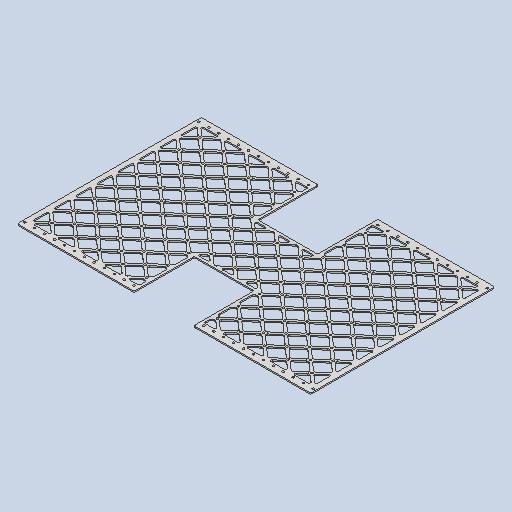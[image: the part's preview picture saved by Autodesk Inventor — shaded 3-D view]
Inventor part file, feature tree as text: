
AUTODESK INVENTOR PART (.ipt)
format: ipt  version: 2023 (Build 270158000, 158)  size: 3,945,984 bytes
history: native  units: in
note: dims shown in document units (in); Inventor stores cm internally (conversion verified against a paired STEP export)
features: extrude x10, sketch x6, pattern_linear x3, fillet x2, plane x1, mirror x1
ambient origin geometry x8: Origin, YZ Plane, XZ Plane, XY Plane, X Axis, Y Axis, Z Axis, Center Point
bodies: Solid1 (feature_tree)
feature tree (23):
  extrude  "Extrusion1"  Depth=0.5in
  sketch  "Sketch2"  dims[d6=0.25in d7=0.5in]
  extrude  "Extrusion2"  Depth=0.5in
  pattern_linear  "Rectangular Pattern1"  Spacing1=2.125in  [1 undecoded]
  extrude  "Extrusion3"  Depth=0.25in
  sketch  "Sketch4"  dims[d10=17.0in]
  sketch  "Sketch7"  dims[d11=28.5in]
  extrude  "Extrusion10"  Depth=0.25in
  extrude  "Extrusion11"  TaperAngle=0.0deg  [1 undecoded]
  extrude  "Extrusion12"  Depth=0.125in
  extrude  "Extrusion13"  Depth=0.125in
  pattern_linear  "Rectangular Pattern2"  Spacing1=0.5in  [1 undecoded]
  pattern_linear  "Rectangular Pattern3"  Spacing1=0.5in  [1 undecoded]
  extrude  "Extrusion7"  TaperAngle=0.0deg  [1 undecoded]
  extrude  "Extrusion8"  Depth=0.25in
  plane  "Work Plane2"
  extrude  "Extrusion14"  Depth=0.25in
  mirror  "Mirror3"
  fillet  "Fillet1"  Radius=0.25in
  fillet  "Fillet2"  Radius=0.25in
  sketch  "Sketch1"  dims[d2=0.25in d4=0.5in]
  sketch  "Sketch3"  dims[d8=0.125in d9=0.0in]
  sketch  "Sketch8"  dims[d12=2.375in d13=2.125in d14=0.25in d15=0.25in d16=0.0in d17=0.0in d18=3.1496in d20=2.125in d21=4.7244in d23=-2.375in d24=0.5in d25=0.5in d26=0.0in d27=0.0in d32=0.25in d40=0.25in d41=0.25in d42=0.25in d43=0.0in d44=0.0in d45=0.0in d46=0.0in d49=0.21in d50=0.5in d51=0.21in d52=0.5in d53=0.0in d54=0.0in d55=1.0in d56=0.0in d57=1.0in d58=0.0in d59=1.0in d60=0.0in d61=3.1496in d63=2.125in d64=4.7244in d66=-2.375in d67=2.7559in d69=2.125in d70=4.3307in d72=-2.375in d73=1.0in d74=0.0in d75=0.125in d76=0.125in d77=0.125in]
note: 5 required parameter values undecoded (feature->parameter linkage not recoverable at this tier; creation-order binding heuristic only, values carry confidence <= 0.55)
